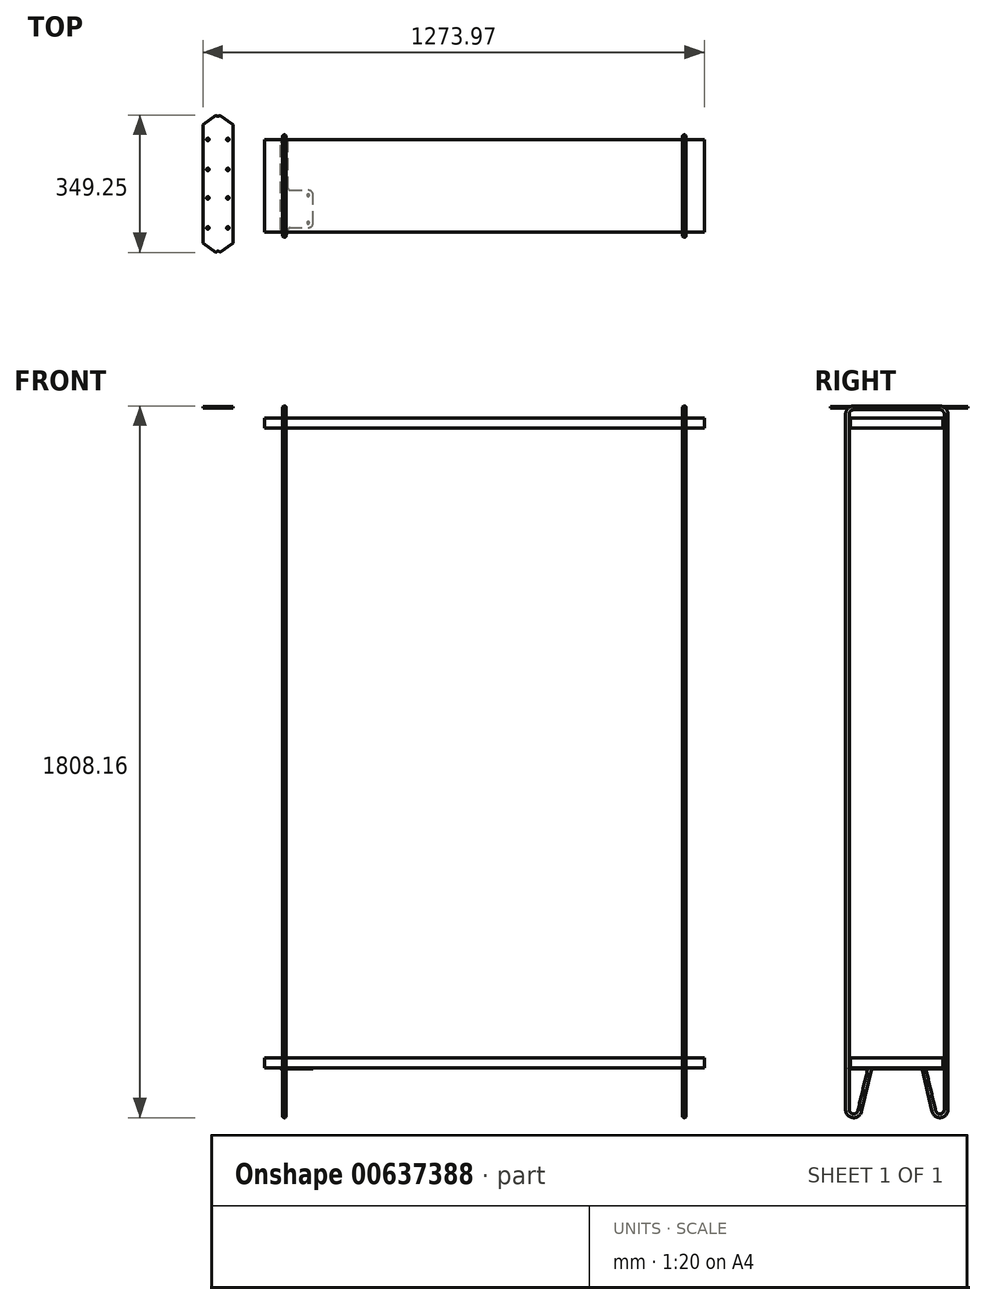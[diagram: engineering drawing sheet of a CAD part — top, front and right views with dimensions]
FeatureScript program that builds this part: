
annotation { "Feature Type Name" : "Feature", "Feature Type Description" : "" }
export const myFeature = defineFeature(function(context is Context, id is Id, definition is map)
    precondition{}
    {
        {
            var Q0;
            Q0=qCreatedBy(makeId("Right.planeOp"),FACE);
            var sketch = newSketch(context, id + "F0", { "sketchPlane" : qUnion([Q0])});
            skLineSegment(sketch, "E0", {"start": v(0, 0) * mm, "end": v(-109.54, 0) * mm});
            skLineSegment(sketch, "E1", {"start": v(-125.41, -15.87) * mm, "end": v(-125.41, -1782.76) * mm});
            skLineSegment(sketch, "E2", {"start": v(-94.08, -1786.4) * mm, "end": v(-68.26, -1676.4) * mm});
            skLineSegment(sketch, "E3.bottom", {"start": v(-117.48, -1651) * mm, "end": v(117.47, -1651) * mm, "construction": true});
            skLineSegment(sketch, "E3.top", {"start": v(-117.47, -1676.4) * mm, "end": v(117.47, -1676.4) * mm, "construction": true});
            skLineSegment(sketch, "E3.left", {"start": v(-117.48, -1651) * mm, "end": v(-117.48, -1676.4) * mm, "construction": true});
            skLineSegment(sketch, "E3.right", {"start": v(117.47, -1651) * mm, "end": v(117.47, -1676.4) * mm, "construction": true});
            skLineSegment(sketch, "E4.bottom", {"start": v(-117.48, -25.4) * mm, "end": v(117.48, -25.4) * mm, "construction": true});
            skLineSegment(sketch, "E4.top", {"start": v(-117.48, -50.8) * mm, "end": v(117.48, -50.8) * mm, "construction": true});
            skLineSegment(sketch, "E4.left", {"start": v(-117.48, -25.4) * mm, "end": v(-117.48, -50.8) * mm, "construction": true});
            skLineSegment(sketch, "E4.right", {"start": v(117.47, -25.4) * mm, "end": v(117.47, -50.8) * mm, "construction": true});
            skLineSegment(sketch, "E5", {"start": v(-676.51, -1803.4) * mm, "end": v(1353.32, -1803.4) * mm, "construction": true});
            skArc(sketch, "E6", {"start": v(-125.41, -1782.76) * mm, "mid": v(-111.36, -1798.53) * mm, "end": v(-94.08, -1786.4) * mm});
            skArc(sketch, "E7", {"start": v(-109.54, 0) * mm, "mid": v(-120.76, -4.65) * mm, "end": v(-125.41, -15.87) * mm});
            skLineSegment(sketch, "E8", {"start": v(0, -25.4) * mm, "end": v(0, 117.18) * mm, "construction": true});
            skLineSegment(sketch, "E9.MirrorCS", {"start": v(0, 0) * mm, "end": v(109.54, 0) * mm});
            skArc(sketch, "E10.MirrorCS", {"start": v(109.54, 0) * mm, "mid": v(120.76, -4.65) * mm, "end": v(125.41, -15.87) * mm});
            skLineSegment(sketch, "E11.MirrorCS", {"start": v(125.41, -15.87) * mm, "end": v(125.41, -1782.76) * mm});
            skArc(sketch, "E12.MirrorCS", {"start": v(125.41, -1782.76) * mm, "mid": v(111.36, -1798.53) * mm, "end": v(94.08, -1786.4) * mm});
            skLineSegment(sketch, "E13.MirrorCS", {"start": v(94.08, -1786.4) * mm, "end": v(68.26, -1676.4) * mm});
            skLineSegment(sketch, "E14.0", {"start": v(-98.72, -1785.3) * mm, "end": v(-71.87, -1670.91) * mm, "construction": true});
            skArc(sketch, "E14.1", {"start": v(-120.65, -1782.76) * mm, "mid": v(-110.82, -1793.8) * mm, "end": v(-98.72, -1785.3) * mm, "construction": true});
            skLineSegment(sketch, "E14.2", {"start": v(-120.65, -15.87) * mm, "end": v(-120.65, -1782.76) * mm, "construction": true});
            skArc(sketch, "E14.3", {"start": v(-109.54, -4.76) * mm, "mid": v(-117.4, -8.02) * mm, "end": v(-120.65, -15.87) * mm, "construction": true});
            skLineSegment(sketch, "E14.4", {"start": v(0, -4.76) * mm, "end": v(-109.54, -4.76) * mm, "construction": true});
            skLineSegment(sketch, "E14.5", {"start": v(0, -4.76) * mm, "end": v(109.54, -4.76) * mm, "construction": true});
            skLineSegment(sketch, "E14.6", {"start": v(98.72, -1785.3) * mm, "end": v(49.43, -1575.34) * mm, "construction": true});
            skArc(sketch, "E14.7", {"start": v(120.65, -1782.76) * mm, "mid": v(110.82, -1793.8) * mm, "end": v(98.72, -1785.3) * mm, "construction": true});
            skLineSegment(sketch, "E14.8", {"start": v(120.65, -15.87) * mm, "end": v(120.65, -1782.76) * mm, "construction": true});
            skArc(sketch, "E14.9", {"start": v(109.54, -4.76) * mm, "mid": v(117.4, -8.02) * mm, "end": v(120.65, -15.87) * mm, "construction": true});
            skLineSegment(sketch, "E15.0", {"start": v(-89.45, -1787.48) * mm, "end": v(-63.56, -1677.2) * mm, "construction": true});
            skArc(sketch, "E15.1", {"start": v(-130.18, -1782.76) * mm, "mid": v(-111.91, -1803.26) * mm, "end": v(-89.45, -1787.48) * mm, "construction": true});
            skLineSegment(sketch, "E15.2", {"start": v(-130.18, -15.87) * mm, "end": v(-130.18, -1782.76) * mm, "construction": true});
            skArc(sketch, "E15.3", {"start": v(-109.54, 4.76) * mm, "mid": v(-124.13, -1.28) * mm, "end": v(-130.18, -15.87) * mm, "construction": true});
            skLineSegment(sketch, "E15.4", {"start": v(0, 4.76) * mm, "end": v(-109.54, 4.76) * mm, "construction": true});
            skLineSegment(sketch, "E15.5", {"start": v(0, 4.76) * mm, "end": v(109.54, 4.76) * mm, "construction": true});
            skLineSegment(sketch, "E15.6", {"start": v(89.45, -1787.48) * mm, "end": v(62.8, -1674) * mm, "construction": true});
            skArc(sketch, "E15.7", {"start": v(130.18, -1782.76) * mm, "mid": v(111.91, -1803.26) * mm, "end": v(89.45, -1787.48) * mm, "construction": true});
            skLineSegment(sketch, "E15.8", {"start": v(130.18, -15.87) * mm, "end": v(130.18, -1782.76) * mm, "construction": true});
            skArc(sketch, "E15.9", {"start": v(109.54, 4.76) * mm, "mid": v(124.13, -1.28) * mm, "end": v(130.18, -15.87) * mm, "construction": true});
            skSolve(sketch);
        }
        {
            var Q0;
            Q0=qCreatedBy(makeId("Front.planeOp"),FACE);
            var sketch = newSketch(context, id + "F1", { "sketchPlane" : qUnion([Q0])});
            skCircle(sketch, "E16", {"center": v(0, 0) * mm, "radius": 4.76 * mm});
            skSolve(sketch);
        }
        {
            var Q0;
            Q0=qSketchRegion(id+"F1",true);
            var Q1;
            Q1=qConstructionFilter(qBodyType(qCreatedBy(id+"F0",EDGE),BodyType.WIRE),ConstructionObject.NO);
            sweep(context, id + "F2", {"profiles" : qUnion([Q0]), "path" : qUnion([Q1])});
        }
        {
            var Q0;
            Q0=qCreatedBy(makeId("Right.planeOp"),FACE);
            cPlane(context, id + "F3", {"entities" : qUnion([Q0]), "cplaneType" : CPlaneType.OFFSET, "offset" : 508 * mm, "width" : 152.4 * mm, "height" : 152.4 * mm});
        }
        {
            var Q0;
            Q0=makeQuery(id+"F2.opSweep","SWEPT_BODY",BODY,{"disambiguationData":[OSD([sQuery(id+"F0.wireOp",EDGE,"E13.MirrorCS"),sQuery(id+"F1.wireOp",EDGE,"E16")])]});
            var Q1;
            Q1=qCreatedBy(id+"F3.planeOp",FACE);
            mirror(context, id + "F4", {"entities" : qUnion([Q0]), "mirrorPlane" : qUnion([Q1])});
        }
        {
            var Q0;
            Q0=qCreatedBy(id+"F3.planeOp",FACE);
            var sketch = newSketch(context, id + "F5", { "sketchPlane" : qUnion([Q0])});
            skLineSegment(sketch, "E17.0", {"start": v(-117.48, -25.4) * mm, "end": v(117.48, -25.4) * mm});
            skLineSegment(sketch, "E18.0", {"start": v(-117.48, -50.8) * mm, "end": v(117.48, -50.8) * mm});
            skLineSegment(sketch, "E19.0", {"start": v(117.47, -25.4) * mm, "end": v(117.47, -50.8) * mm});
            skLineSegment(sketch, "E20.0", {"start": v(-117.48, -25.4) * mm, "end": v(-117.48, -50.8) * mm});
            skLineSegment(sketch, "E21.0", {"start": v(-117.48, -1651) * mm, "end": v(-117.48, -1676.4) * mm});
            skLineSegment(sketch, "E22.0", {"start": v(-117.47, -1676.4) * mm, "end": v(117.47, -1676.4) * mm});
            skLineSegment(sketch, "E23.0", {"start": v(-117.48, -1651) * mm, "end": v(117.47, -1651) * mm});
            skLineSegment(sketch, "E24.0", {"start": v(117.47, -1651) * mm, "end": v(117.47, -1676.4) * mm});
            skSolve(sketch);
        }
        {
            var Q0;
            Q0=qSketchRegion(id+"F5",true);
            var Q1;
            Q1=qConstructionFilter(qBodyType(qCreatedBy(id+"F5",EDGE),BodyType.WIRE),ConstructionObject.NO);
            extrude(context, id + "F6", {"entities" : qUnion([Q0]), "surfaceEntities" : qUnion([Q1]), "depth" : 558.8 * mm, "offsetDistance" : 25.4 * mm, "hasSecondDirection" : true, "secondDirectionOppositeDirection" : true, "secondDirectionDepth" : 558.8 * mm});
        }
        {
            var Q0;
            Q0=makeQuery(id+"F6.opExtrude","SWEPT_FACE",FACE,{"disambiguationData":[OSD([sQuery(id+"F5.wireOp",EDGE,"E22.0")])]});
            var sketch = newSketch(context, id + "F7", { "sketchPlane" : qUnion([Q0])});
            skArc(sketch, "E25.0", {"start": v(-4.58, 124.12) * mm, "mid": v(0, 120.65) * mm, "end": v(4.58, 124.12) * mm});
            skArc(sketch, "E26.0", {"start": v(2.69, -123.84) * mm, "mid": v(0, -122.3) * mm, "end": v(-2.69, -123.84) * mm});
            skLineSegment(sketch, "E27.left", {"start": v(-9.52, 111.76) * mm, "end": v(-9.52, -111.76) * mm});
            skLineSegment(sketch, "E27.right", {"start": v(9.53, 111.76) * mm, "end": v(9.53, -111.76) * mm});
            skLineSegment(sketch, "E28", {"start": v(-4.58, 124.12) * mm, "end": v(-9.53, 111.76) * mm});
            skLineSegment(sketch, "E29", {"start": v(4.58, 124.12) * mm, "end": v(9.53, 111.76) * mm});
            skLineSegment(sketch, "E30", {"start": v(-2.69, -123.84) * mm, "end": v(-9.52, -111.76) * mm});
            skLineSegment(sketch, "E31", {"start": v(9.53, -111.76) * mm, "end": v(2.69, -123.84) * mm});
            skPoint(sketch, "E32.orphan", {"position": v(9.53, -125.41) * mm});
            skPoint(sketch, "E33.orphan", {"position": v(-9.52, 125.41) * mm});
            skPoint(sketch, "E34.orphan", {"position": v(9.52, 125.41) * mm});
            skLineSegment(sketch, "E35", {"start": v(0, 125.41) * mm, "end": v(0, -125.41) * mm, "construction": true});
            skLineSegment(sketch, "E36", {"start": v(-9.52, 0) * mm, "end": v(9.53, 0) * mm, "construction": true});
            skCircle(sketch, "E37", {"center": v(0, 0) * mm, "radius": 3.18 * mm});
            skCircle(sketch, "E38", {"center": v(0, 44.45) * mm, "radius": 3.18 * mm});
            skCircle(sketch, "E39", {"center": v(0, 95.25) * mm, "radius": 3.18 * mm});
            skCircle(sketch, "E40.MirrorC", {"center": v(0, -44.45) * mm, "radius": 3.18 * mm});
            skCircle(sketch, "E41.MirrorC", {"center": v(0, -95.25) * mm, "radius": 3.18 * mm});
            skLineSegment(sketch, "E42.bottom", {"start": v(9.53, 106.03) * mm, "end": v(60.33, 106.03) * mm});
            skLineSegment(sketch, "E42.top", {"start": v(9.53, 10.7) * mm, "end": v(60.33, 10.7) * mm});
            skLineSegment(sketch, "E42.left", {"start": v(9.53, 106.03) * mm, "end": v(9.53, 10.7) * mm});
            skLineSegment(sketch, "E42.right", {"start": v(73.03, 93.33) * mm, "end": v(73.03, 23.4) * mm});
            skLineSegment(sketch, "E43", {"start": v(60.33, 10.7) * mm, "end": v(60.32, 106.03) * mm, "construction": true});
            skCircle(sketch, "E44", {"center": v(60.33, 23.4) * mm, "radius": 3.18 * mm});
            skCircle(sketch, "E45", {"center": v(60.32, 93.33) * mm, "radius": 3.18 * mm});
            skPoint(sketch, "E46.visualSharp", {"position": v(73.03, 106.03) * mm});
            skArc(sketch, "E46.filletArc", {"start": v(73.03, 93.33) * mm, "mid": v(69.3, 102.3) * mm, "end": v(60.33, 106.03) * mm});
            skPoint(sketch, "E47.visualSharp", {"position": v(73.03, 10.7) * mm});
            skArc(sketch, "E47.filletArc", {"start": v(60.33, 10.7) * mm, "mid": v(69.3, 14.42) * mm, "end": v(73.03, 23.4) * mm});
            skPoint(sketch, "E48", {"position": v(0, -122.3) * mm});
            skPoint(sketch, "E49", {"position": v(0, 120.65) * mm});
            skSolve(sketch);
        }
        {
            var Q0;
            Q0=qSketchRegion(id+"F7",true);
            extrude(context, id + "F8", {"entities" : qUnion([Q0]), "depth" : 3.17 * mm, "offsetDistance" : 25.4 * mm});
        }
        {
            var Q0;
            Q0=makeQuery(id+"F8.opExtrude","SWEPT_EDGE",EDGE,{"disambiguationData":[OSD([sQuery(id+"F7.wireOp",EDGE,"E25.0"),sQuery(id+"F7.wireOp",EDGE,"E29")])]});
            var Q1;
            Q1=makeQuery(id+"F8.opExtrude","SWEPT_EDGE",EDGE,{"disambiguationData":[OSD([sQuery(id+"F7.wireOp",EDGE,"E26.0"),sQuery(id+"F7.wireOp",EDGE,"E31")])]});
            var Q2;
            Q2=makeQuery(id+"F8.opExtrude","SWEPT_EDGE",EDGE,{"disambiguationData":[OSD([sQuery(id+"F7.wireOp",EDGE,"E26.0"),sQuery(id+"F7.wireOp",EDGE,"E30")])]});
            var Q3;
            Q3=makeQuery(id+"F8.opExtrude","SWEPT_EDGE",EDGE,{"disambiguationData":[OSD([sQuery(id+"F7.wireOp",EDGE,"E25.0"),sQuery(id+"F7.wireOp",EDGE,"E28")])]});
            fillet(context, id + "F9", {"entities" : qUnion([Q0, Q1, Q2, Q3]), "radius" : 0.64 * mm, "tangentPropagation" : true, "defaultsChanged" : false, "vertexSettings" : [], "allowEdgeOverflow" : false});
        }
        {
            var Q0;
            Q0=makeQuery(id+"F8.opExtrude","SWEPT_EDGE",EDGE,{"disambiguationData":[OSD([sQuery(id+"F5.wireOp",EDGE,"E22.0"),sQuery(id+"F5.wireOp",EDGE,"E24.0"),sQuery(id+"F7.wireOp",EDGE,"E27.left"),sQuery(id+"F7.wireOp",EDGE,"E30")])]});
            var Q1;
            Q1=makeQuery(id+"F8.opExtrude","SWEPT_EDGE",EDGE,{"disambiguationData":[OSD([sQuery(id+"F5.wireOp",EDGE,"E22.0"),sQuery(id+"F5.wireOp",EDGE,"E24.0"),sQuery(id+"F7.wireOp",EDGE,"E27.right"),sQuery(id+"F7.wireOp",EDGE,"E31")])]});
            var Q2;
            Q2=makeQuery(id+"F8.opExtrude","SWEPT_EDGE",EDGE,{"disambiguationData":[OSD([sQuery(id+"F5.wireOp",EDGE,"E21.0"),sQuery(id+"F5.wireOp",EDGE,"E22.0"),sQuery(id+"F7.wireOp",EDGE,"E27.right"),sQuery(id+"F7.wireOp",EDGE,"E29")])]});
            var Q3;
            Q3=makeQuery(id+"F8.opExtrude","SWEPT_EDGE",EDGE,{"disambiguationData":[OSD([sQuery(id+"F5.wireOp",EDGE,"E21.0"),sQuery(id+"F5.wireOp",EDGE,"E22.0"),sQuery(id+"F7.wireOp",EDGE,"E27.left"),sQuery(id+"F7.wireOp",EDGE,"E28")])]});
            fillet(context, id + "F10", {"entities" : qUnion([Q0, Q1, Q2, Q3]), "radius" : 6.35 * mm, "tangentPropagation" : true, "allowEdgeOverflow" : false});
        }
        {
            var Q0;
            Q0=makeQuery(id+"F8.opExtrude","SWEPT_EDGE",EDGE,{"disambiguationData":[OSD([sQuery(id+"F7.wireOp",EDGE,"E27.right"),sQuery(id+"F7.wireOp",EDGE,"E42.top"),sQuery(id+"F7.wireOp",EDGE,"E42.left")])]});
            var Q1;
            Q1=makeQuery(id+"F8.opExtrude","SWEPT_EDGE",EDGE,{"disambiguationData":[OSD([sQuery(id+"F7.wireOp",EDGE,"E27.right"),sQuery(id+"F7.wireOp",EDGE,"E42.bottom"),sQuery(id+"F7.wireOp",EDGE,"E42.left")])]});
            fillet(context, id + "F11", {"entities" : qUnion([Q0, Q1]), "tangentPropagation" : true, "radius" : 5.08 * mm, "defaultsChanged" : false, "vertexSettings" : [], "allowEdgeOverflow" : false});
        }
        {
            var Q0;
            Q0=qCreatedBy(makeId("Top.planeOp"),FACE);
            var sketch = newSketch(context, id + "F12", { "sketchPlane" : qUnion([Q0])});
            skLineSegment(sketch, "E50.top", {"start": v(-207.17, 5.74) * mm, "end": v(-130.97, 5.74) * mm});
            skLineSegment(sketch, "E50.left", {"start": v(-207.17, 156.23) * mm, "end": v(-207.17, 5.74) * mm});
            skLineSegment(sketch, "E50.right", {"start": v(-130.97, 156.23) * mm, "end": v(-130.97, 5.74) * mm});
            skArc(sketch, "E51", {"start": v(-173.66, 180.36) * mm, "mid": v(-169.07, 176.87) * mm, "end": v(-164.48, 180.36) * mm});
            skPoint(sketch, "E51.centerSnap0", {"position": v(-169.07, 180.36) * mm});
            skLineSegment(sketch, "E52", {"start": v(-173.66, 180.36) * mm, "end": v(-207.17, 156.23) * mm});
            skLineSegment(sketch, "E53", {"start": v(-164.48, 180.36) * mm, "end": v(-130.97, 156.23) * mm});
            skPoint(sketch, "E54.orphan", {"position": v(-130.97, 180.36) * mm});
            skPoint(sketch, "E50.bottom.start.orphan", {"position": v(-207.17, 180.36) * mm});
            skLineSegment(sketch, "E55", {"start": v(-194.47, 156.23) * mm, "end": v(-194.47, 5.74) * mm, "construction": true});
            skLineSegment(sketch, "E56", {"start": v(-169.07, 181.63) * mm, "end": v(-169.07, 5.74) * mm, "construction": true});
            skCircle(sketch, "E57", {"center": v(-194.47, 118.13) * mm, "radius": 3.18 * mm});
            skCircle(sketch, "E58", {"center": v(-194.47, 41.93) * mm, "radius": 3.18 * mm});
            skCircle(sketch, "E59.MirrorC", {"center": v(-143.67, 118.13) * mm, "radius": 3.18 * mm});
            skCircle(sketch, "E60.MirrorC", {"center": v(-143.67, 41.93) * mm, "radius": 3.18 * mm});
            skLineSegment(sketch, "E61.MirrorCS", {"start": v(-130.97, -144.76) * mm, "end": v(-130.97, 5.74) * mm});
            skLineSegment(sketch, "E62.MirrorCS", {"start": v(-164.48, -168.89) * mm, "end": v(-130.97, -144.76) * mm});
            skLineSegment(sketch, "E63.MirrorCS", {"start": v(-173.66, -168.89) * mm, "end": v(-207.17, -144.76) * mm});
            skLineSegment(sketch, "E64.MirrorCS", {"start": v(-207.17, -144.76) * mm, "end": v(-207.17, 5.74) * mm});
            skCircle(sketch, "E65.MirrorC", {"center": v(-194.47, -106.66) * mm, "radius": 3.18 * mm});
            skCircle(sketch, "E66.MirrorC", {"center": v(-194.47, -30.46) * mm, "radius": 3.18 * mm});
            skCircle(sketch, "E67.MirrorC", {"center": v(-143.67, -30.46) * mm, "radius": 3.18 * mm});
            skCircle(sketch, "E68.MirrorC", {"center": v(-143.67, -106.66) * mm, "radius": 3.18 * mm});
            skArc(sketch, "E69.MirrorCS", {"start": v(-173.66, -168.89) * mm, "mid": v(-169.07, -165.4) * mm, "end": v(-164.48, -168.89) * mm});
            skPoint(sketch, "E70", {"position": v(-169.07, 176.87) * mm});
            skPoint(sketch, "E71", {"position": v(-169.07, -165.4) * mm});
            skSolve(sketch);
        }
        {
            var Q0;
            Q0 = qSketchRegion(id + "F12", true);
            extrude(context, id + "F13", {"entities" : qUnion([Q0]), "depth" : 3.17 * mm, "offsetDistance" : 25.4 * mm});
        }
    });
